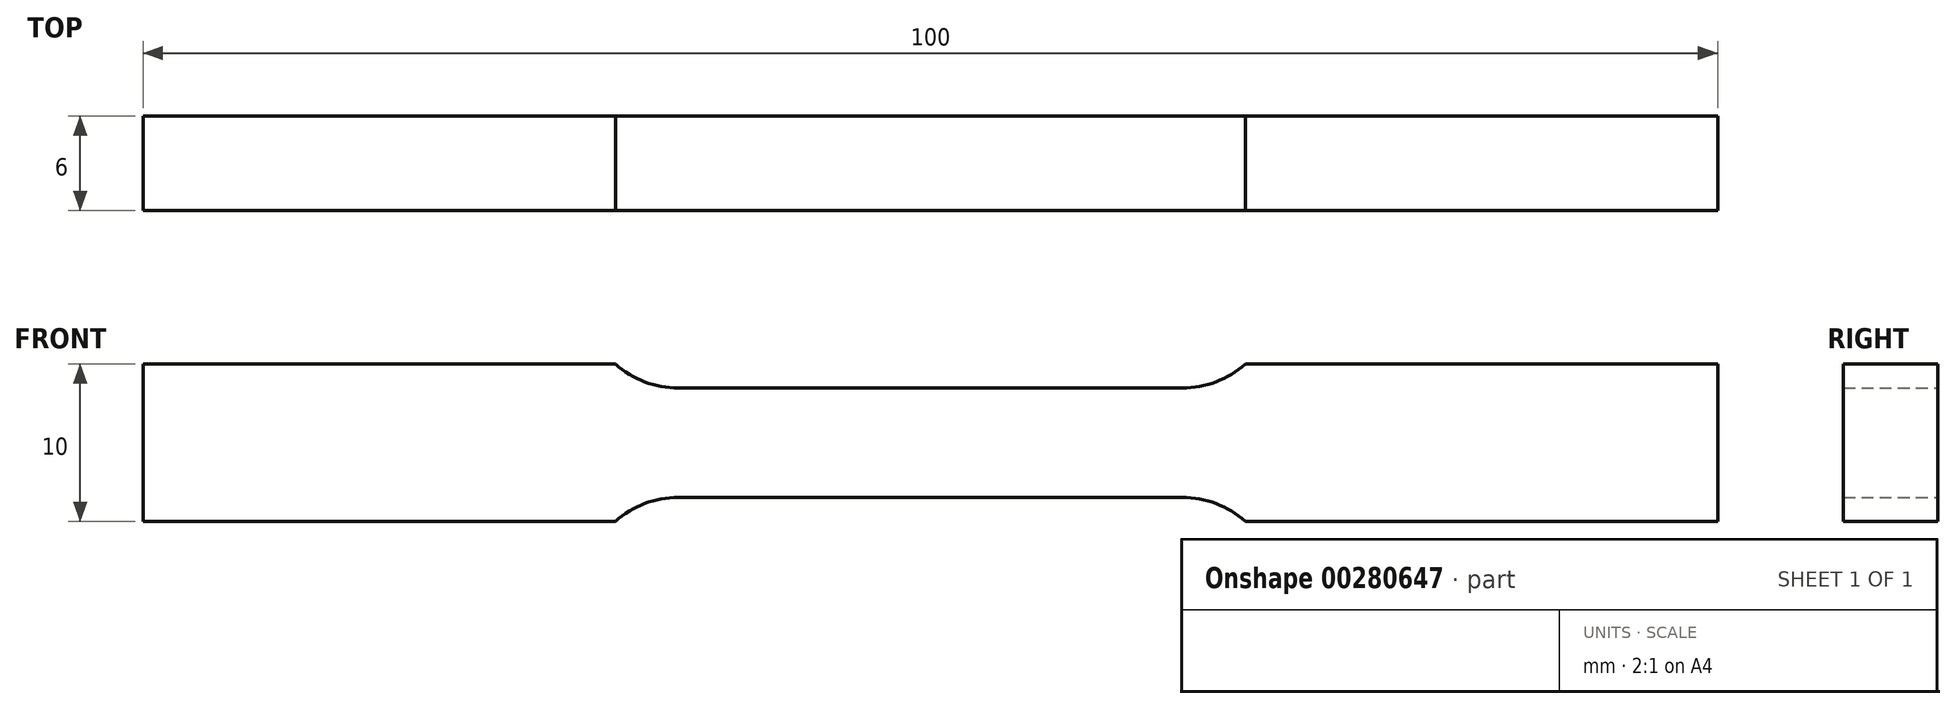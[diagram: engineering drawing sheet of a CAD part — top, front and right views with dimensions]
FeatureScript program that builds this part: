
annotation { "Feature Type Name" : "Feature", "Feature Type Description" : "" }
export const myFeature = defineFeature(function(context is Context, id is Id, definition is map)
    precondition{}
    {
        {
            var Q0;
            Q0=qCreatedBy(makeId("Front.planeOp"),FACE);
            var sketch = newSketch(context, id + "F0", { "sketchPlane" : qUnion([Q0])});
            skLineSegment(sketch, "E0", {"start": v(0, 3.47) * mm, "end": v(16, 3.47) * mm});
            skArc(sketch, "E1", {"start": v(16, 3.47) * mm, "mid": v(18.14, 3.87) * mm, "end": v(20, 5) * mm});
            skLineSegment(sketch, "E2", {"start": v(20, 5) * mm, "end": v(50, 5) * mm});
            skLineSegment(sketch, "E3", {"start": v(50, 5) * mm, "end": v(50, 0) * mm});
            skLineSegment(sketch, "E4.MirrorCS", {"start": v(0, -3.47) * mm, "end": v(16, -3.47) * mm});
            skArc(sketch, "E5.MirrorCS", {"start": v(16, -3.47) * mm, "mid": v(18.14, -3.87) * mm, "end": v(20, -5) * mm});
            skLineSegment(sketch, "E6.MirrorCS", {"start": v(20, -5) * mm, "end": v(50, -5) * mm});
            skLineSegment(sketch, "E7.MirrorCS", {"start": v(50, -5) * mm, "end": v(50, 0) * mm});
            skLineSegment(sketch, "E8.MirrorCS", {"start": v(0, 3.47) * mm, "end": v(-16, 3.47) * mm});
            skArc(sketch, "E9.MirrorCS", {"start": v(-16, 3.47) * mm, "mid": v(-18.14, 3.87) * mm, "end": v(-20, 5) * mm});
            skLineSegment(sketch, "E10.MirrorCS", {"start": v(-20, 5) * mm, "end": v(-50, 5) * mm});
            skLineSegment(sketch, "E11.MirrorCS", {"start": v(-50, 5) * mm, "end": v(-50, 0) * mm});
            skLineSegment(sketch, "E12.MirrorCS", {"start": v(-50, -5) * mm, "end": v(-50, 0) * mm});
            skLineSegment(sketch, "E13.MirrorCS", {"start": v(-20, -5) * mm, "end": v(-50, -5) * mm});
            skArc(sketch, "E14.MirrorCS", {"start": v(-16, -3.47) * mm, "mid": v(-18.14, -3.87) * mm, "end": v(-20, -5) * mm});
            skLineSegment(sketch, "E15.MirrorCS", {"start": v(0, -3.47) * mm, "end": v(-16, -3.47) * mm});
            skSolve(sketch);
        }
        {
            var Q0;
            Q0 = qSketchRegion(id + "F0", true);
            extrude(context, id + "F1", {"entities" : qUnion([Q0]), "endBound" : BoundingType.SYMMETRIC, "depth" : 6 * mm});
        }
    });
